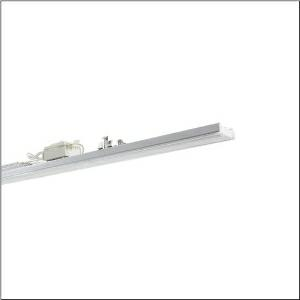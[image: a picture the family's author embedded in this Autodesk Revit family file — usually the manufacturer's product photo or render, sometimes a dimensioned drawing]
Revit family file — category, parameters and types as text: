
# Revit family: licross_r__21_recessed_mo_52tl19mn1axg_622b
name_source: partatom
category: Lighting Fixtures
units: mm (PartAtom-declared; Revit-internal decimal feet)

## family parameters
Cut with Voids When Loaded = No
Host = Face
Light Source = No
Part Type = Normal
Room Calculation Point = No
Round Connector Dimension = Use Diameter
Shared = No

## types (1)
- --- (1 x LED, 10200 lm, 60.5 W, 3500K)
    Apparent Load = 61 VA
    CIE Flux Codes = 55 90 98 100 100
    Color Rendering = 80
    Color Temperature = 3500K
    Default Elevation = 1800 mm
    Description = Licross® 21 Recessed MO, luminaire insert, of sheet steel, galvanised, coil coated, white, length: 1.500mm, width: 66mm, height: 67mm, LED rated luminous flux: 10.200lm, light colour: 835, control gear: ON/OFF Multilumen, with plug, 3-pole, with phase selection, mains connection: 220..240V, AC, 50/60Hz, rated input power: 60.5W, internal wiring halogen-free, primary light control with lens, of plastic, primary optical cover: cover, of PMMA, light emission: direct distribution, primary light characteristic: double asymmetric, protection rating (complete): IP40, insulation class (complete): insulation class I (protective earthing), certification: CE, ENEC, VDE, UKCA, protection symbol: D if used in an environment without relevant dust loads with corresponding accessories, impact resistance: IK06, permissible ambient temperature for indoor applications: -25..+35°C, corresponds to IFS (International Featured Standards) requirements for safety and quality in the food industry, reducing of maximum allowable ambient temperature of 5°C with ceiling mounting, LABS conformity tested according to VDMA 24364:2018-05, packaging unit: 1 piece
    Height = 58 mm
    Lamp = 1 x LED
    Lamp Light Flux = 10200 lm
    Lamp Power = 60.5 W
    Lamp count = 1
    Length = 1500 mm
    Luminous efficacy = 169 lm/W
    Manufacturer = Siteco
    ModVariant = No
    Model = 52TL19MN1AXG
    Mounting Place = Ceiling
    Mounting Type = Pendant
    Number of Poles = 1
    OnlyDefault = Yes
    Power Factor = 1
    Product Name = Licross® 21 Recessed MO
    Product group = luminaire insert | ceiling pendant
    ProductGroupID = 902
    Protection Class = Protection class I
    Protection Degree = IP 40
    RLX_Detail_Level = 1
    RLX_Emergency_Light_Flux = 0 lm
    RLX_Emergency_Type = 0
    RLX_Emergency_Type_DB = No
    RlxData = <blob elided: 22257 chars, md5=11e7d0fb>
    Socket = socket
    Standby Power = 0 W
    System Light Flux = 10200 lm
    System Power = 61 W
    Type Comments = factory setting: luminous flux: 100 % | (A | C | E) | 140 mA
    Type Image = l_1296930.jpg
    URL = http://relux.com
    VarID = @adj_089403
    Voltage = 0 V
    Weight = 0.00 kg
    Width = 66 mm

## geometry (parser evidence)
native form markers: Blend x4, Sweep x12
no freeform markers — native parametric forms only
